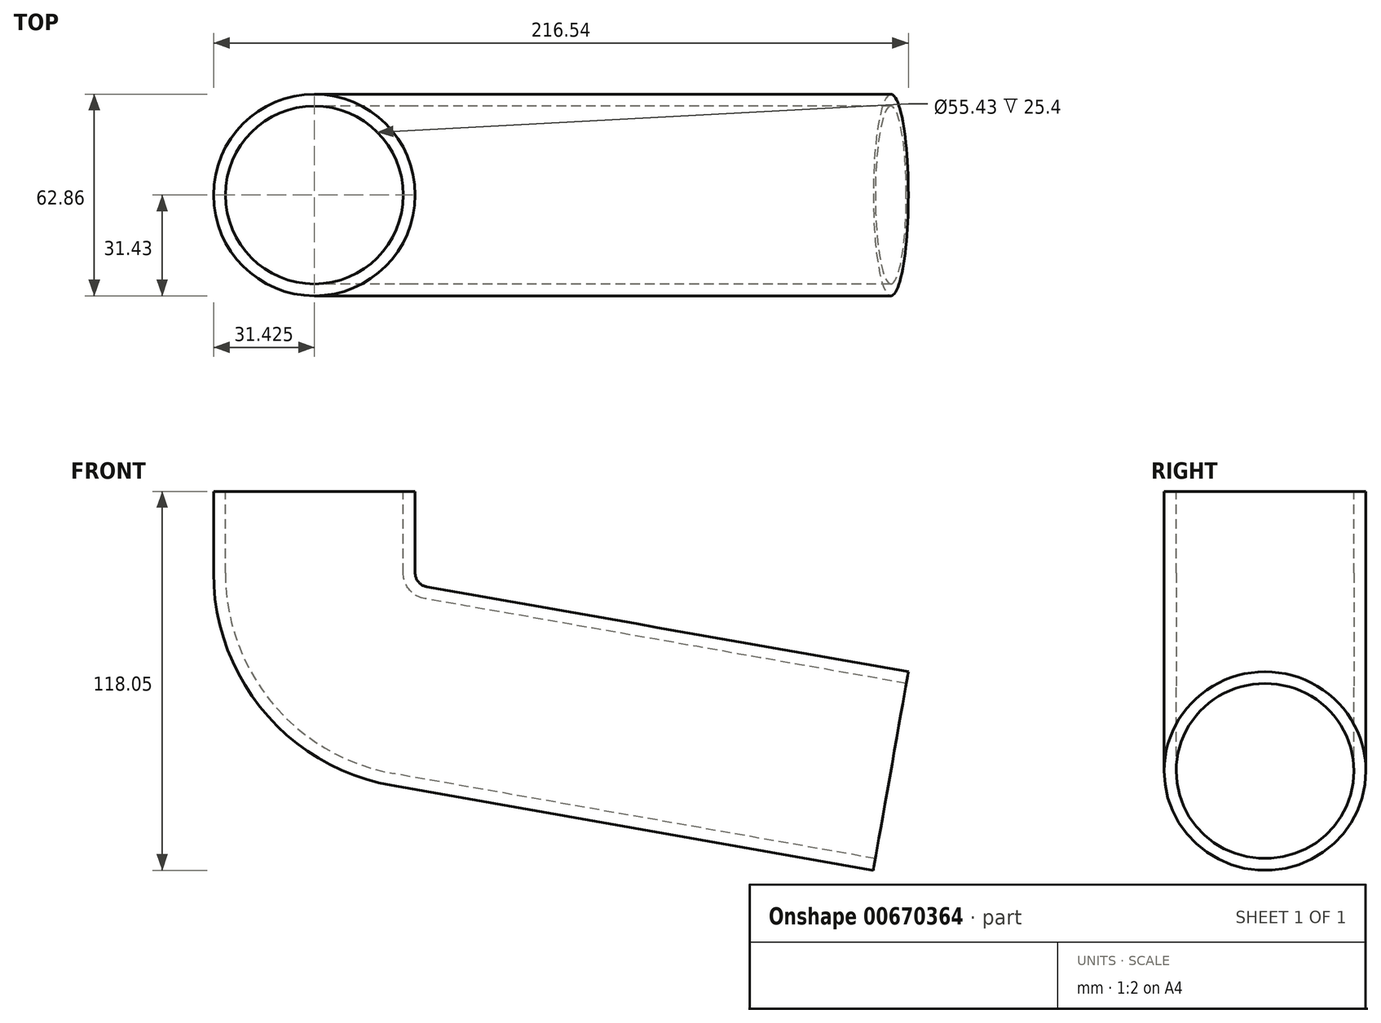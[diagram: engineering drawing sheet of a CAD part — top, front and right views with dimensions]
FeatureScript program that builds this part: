
annotation { "Feature Type Name" : "Feature", "Feature Type Description" : "" }
export const myFeature = defineFeature(function(context is Context, id is Id, definition is map)
    precondition{}
    {
        {
            var Q0;
            Q0=qCreatedBy(makeId("Front.planeOp"),FACE);
            var sketch = newSketch(context, id + "F0", { "sketchPlane" : qUnion([Q0])});
            skLineSegment(sketch, "E0", {"start": v(0, 0) * mm, "end": v(-35.56, 0) * mm, "construction": true});
            skLineSegment(sketch, "E1", {"start": v(0, 0) * mm, "end": v(-6.17, -35.02) * mm, "construction": true});
            skArc(sketch, "E2", {"start": v(-35.56, 0) * mm, "mid": v(-27.24, -22.86) * mm, "end": v(-6.17, -35.02) * mm});
            skLineSegment(sketch, "E3", {"start": v(-35.56, 0) * mm, "end": v(-35.56, 25.4) * mm});
            skLineSegment(sketch, "E4", {"start": v(-6.17, -35.02) * mm, "end": v(143.9, -61.48) * mm});
            skSolve(sketch);
        }
        {
            var Q0;
            Q0=qCreatedBy(makeId("Top.planeOp"),FACE);
            var sketch = newSketch(context, id + "F1", { "sketchPlane" : qUnion([Q0])});
            skCircle(sketch, "E5", {"center": v(-35.79, 0) * mm, "radius": 27.71 * mm});
            skCircle(sketch, "E6", {"center": v(-35.79, 0) * mm, "radius": 31.43 * mm});
            skSolve(sketch);
        }
        {
            var Q0;
            Q0 = qSketchRegion(id + "F1", true);
            var Q1;
            Q1 = qConstructionFilter(qBodyType(qCreatedBy(id + "F1" ,EDGE), BodyType.WIRE), ConstructionObject.NO);
            var Q2;
            Q2 = qConstructionFilter(qBodyType(qCreatedBy(id + "F0" ,EDGE), BodyType.WIRE), ConstructionObject.NO);
            sweep(context, id + "F2", {"profiles" : qUnion([Q0]), "surfaceProfiles" : qUnion([Q1]), "path" : qUnion([Q2])});
        }
        {
            var Q0;
            Q0=sQuery(id+"F1.wireOp",EDGE,"E5");
            var Q1;
            Q1=sQuery(id+"F1.wireOp",EDGE,"E6");
            extrude(context, id + "F3", {"bodyType" : ToolBodyType.SURFACE, "surfaceEntities" : qUnion([Q0, Q1]), "depth" : 25.4 * mm, "offsetDistance" : 25.4 * mm});
        }
    });
